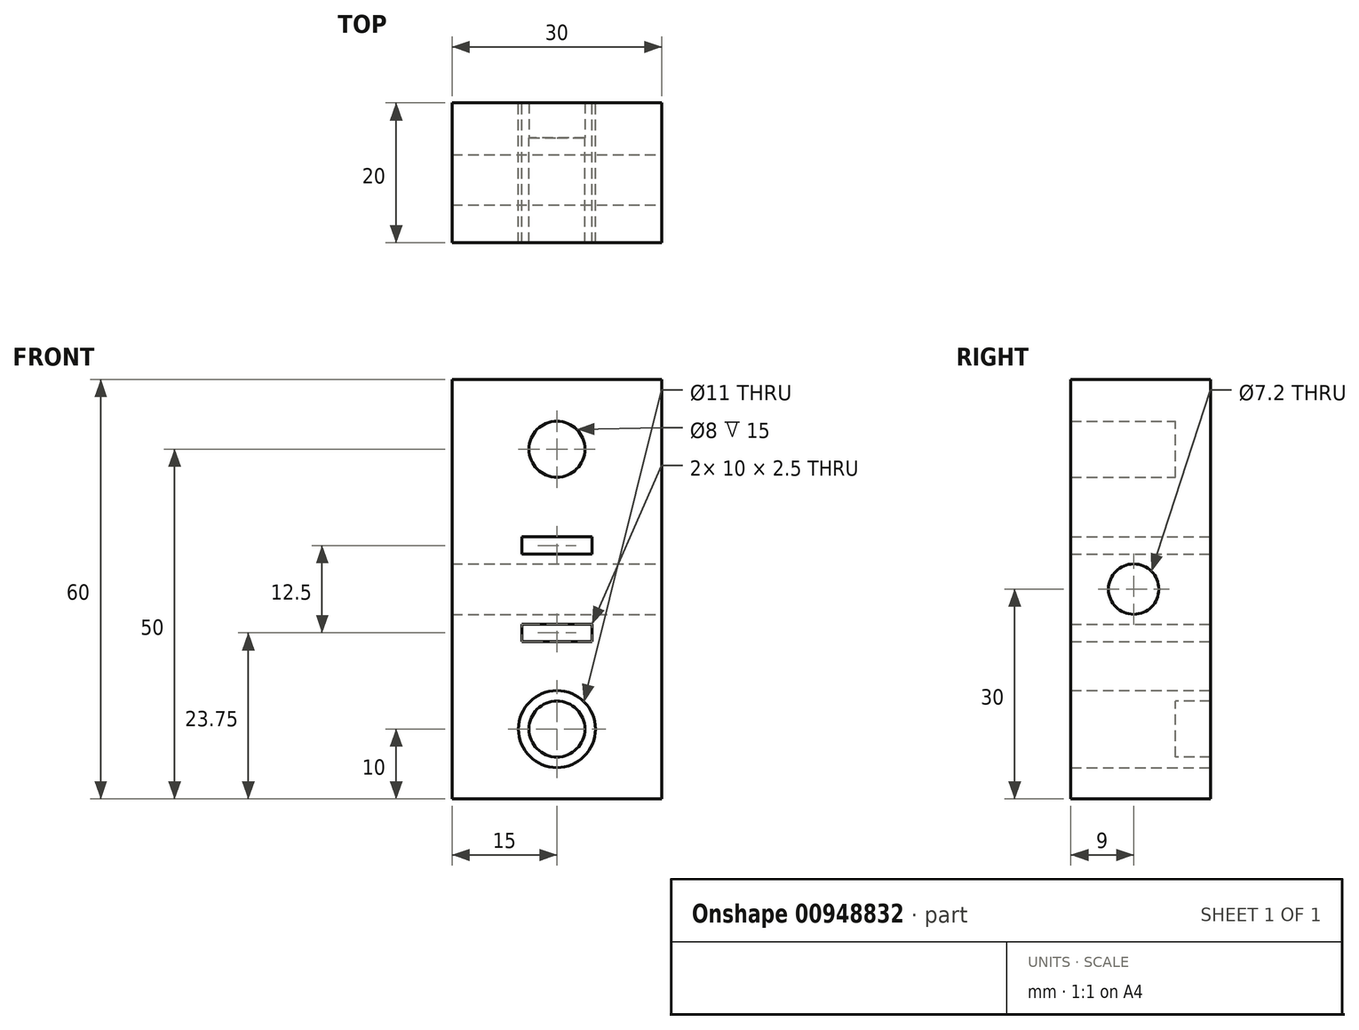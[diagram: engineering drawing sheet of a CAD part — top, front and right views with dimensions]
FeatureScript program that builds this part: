
annotation { "Feature Type Name" : "Feature", "Feature Type Description" : "" }
export const myFeature = defineFeature(function(context is Context, id is Id, definition is map)
    precondition{}
    {
        {
            var Q0;
            Q0=qCreatedBy(makeId("Front.planeOp"),FACE);
            var sketch = newSketch(context, id + "F0", { "sketchPlane" : qUnion([Q0])});
            skLineSegment(sketch, "E0.bottom", {"start": v(15, -30) * mm, "end": v(-15, -30) * mm});
            skLineSegment(sketch, "E0.top", {"start": v(15, 30) * mm, "end": v(-15, 30) * mm});
            skLineSegment(sketch, "E0.left", {"start": v(15, -30) * mm, "end": v(15, 30) * mm});
            skLineSegment(sketch, "E0.right", {"start": v(-15, -30) * mm, "end": v(-15, 30) * mm});
            skPoint(sketch, "E0.middle", {"position": v(0, 0) * mm});
            skCircle(sketch, "E1", {"center": v(0, 20) * mm, "radius": 5.5 * mm});
            skLineSegment(sketch, "E2.bottom", {"start": v(5, 5) * mm, "end": v(-5, 5) * mm});
            skLineSegment(sketch, "E2.top", {"start": v(5, 7.5) * mm, "end": v(-5, 7.5) * mm});
            skLineSegment(sketch, "E2.left", {"start": v(5, 5) * mm, "end": v(5, 7.5) * mm});
            skLineSegment(sketch, "E2.right", {"start": v(-5, 5) * mm, "end": v(-5, 7.5) * mm});
            skPoint(sketch, "E2.middle", {"position": v(0, 6.25) * mm});
            skLineSegment(sketch, "E3.MirrorCS", {"start": v(-5, -5) * mm, "end": v(-5, -7.5) * mm});
            skLineSegment(sketch, "E4.MirrorCS", {"start": v(5, -5) * mm, "end": v(5, -7.5) * mm});
            skLineSegment(sketch, "E5.MirrorCS", {"start": v(5, -7.5) * mm, "end": v(-5, -7.5) * mm});
            skLineSegment(sketch, "E6.MirrorCS", {"start": v(5, -5) * mm, "end": v(-5, -5) * mm});
            skCircle(sketch, "E7.MirrorC", {"center": v(0, -20) * mm, "radius": 5.5 * mm});
            skPoint(sketch, "E8.MirrorP", {"position": v(0, -6.25) * mm});
            skCircle(sketch, "E9", {"center": v(0, 20) * mm, "radius": 4 * mm});
            skCircle(sketch, "E10", {"center": v(0, -20) * mm, "radius": 4 * mm});
            skSolve(sketch);
        }
        {
            var Q0;
            Q0=makeQuery(id+"F0.imprint","IMPRINT",FACE,{"disambiguationData":[TD([[makeQuery(id+"F0.imprint","IMPRINT",EDGE,{"derivedFrom":sQuery(id+"F0.wireOp",EDGE,"E0.bottom")}),-1.0]])]});
            var Q1;
            Q1=makeQuery(id+"F0.imprint","IMPRINT",FACE,{"disambiguationData":[TD([[makeQuery(id+"F0.imprint","IMPRINT",EDGE,{"derivedFrom":sQuery(id+"F0.wireOp",EDGE,"E1")}),1.0]])]});
            var Q2;
            Q2=makeQuery(id+"F0.imprint","IMPRINT",FACE,{"disambiguationData":[TD([[makeQuery(id+"F0.imprint","IMPRINT",EDGE,{"derivedFrom":sQuery(id+"F0.wireOp",EDGE,"E7.MirrorC")}),-1.0]])]});
            extrude(context, id + "F1", {"entities" : qUnion([Q0, Q1, Q2]), "depth" : 5 * mm, "offsetDistance" : 25 * mm});
        }
        {
            var Q0;
            Q0=makeQuery(id+"F0.imprint","IMPRINT",FACE,{"disambiguationData":[TD([[makeQuery(id+"F0.imprint","IMPRINT",EDGE,{"derivedFrom":sQuery(id+"F0.wireOp",EDGE,"E1")}),1.0]])]});
            var Q1;
            Q1=makeQuery(id+"F0.imprint","IMPRINT",FACE,{"disambiguationData":[TD([[makeQuery(id+"F0.imprint","IMPRINT",EDGE,{"derivedFrom":sQuery(id+"F0.wireOp",EDGE,"E7.MirrorC")}),-1.0]])]});
            var Q2;
            Q2=makeQuery(id+"F0.imprint","IMPRINT",FACE,{"disambiguationData":[TD([[makeQuery(id+"F0.imprint","IMPRINT",EDGE,{"derivedFrom":sQuery(id+"F0.wireOp",EDGE,"E9")}),1.0]])]});
            var Q3;
            Q3=makeQuery(id+"F0.imprint","IMPRINT",FACE,{"disambiguationData":[TD([[makeQuery(id+"F0.imprint","IMPRINT",EDGE,{"derivedFrom":sQuery(id+"F0.wireOp",EDGE,"E10")}),1.0]])]});
            var Q4;
            Q4=sQuery(id+"F0.wireOp",EDGE,"E1");
            var Q5;
            Q5=sQuery(id+"F0.wireOp",EDGE,"E7.MirrorC");
            extrude(context, id + "F2", {"entities" : qUnion([Q0, Q1, Q2, Q3]), "operationType" : NewBodyOperationType.ADD, "surfaceEntities" : qUnion([Q4, Q5]), "oppositeDirection" : true, "depth" : 15 * mm, "offsetDistance" : 25 * mm});
        }
        {
            var Q0;
            Q0=qCreatedBy(makeId("Right.planeOp"),FACE);
            var sketch = newSketch(context, id + "F3", { "sketchPlane" : qUnion([Q0])});
            skCircle(sketch, "E11", {"center": v(4, 0) * mm, "radius": 3.6 * mm});
            skLineSegment(sketch, "E12.bottom", {"start": v(0, 5) * mm, "end": v(10, 5) * mm});
            skLineSegment(sketch, "E12.top", {"start": v(0, -5) * mm, "end": v(10, -5) * mm});
            skLineSegment(sketch, "E12.left", {"start": v(0, 5) * mm, "end": v(0, -5) * mm});
            skLineSegment(sketch, "E12.right", {"start": v(10, 5) * mm, "end": v(10, -5) * mm});
            skSolve(sketch);
        }
        {
            var Q0;
            Q0=qSketchRegion(id+"F3",true);
            var Q1;
            Q1=makeQuery(id+"F3.imprint","IMPRINT",FACE,{"disambiguationData":[TD([[makeQuery(id+"F3.imprint","IMPRINT",EDGE,{"derivedFrom":sQuery(id+"F3.wireOp",EDGE,"E11")}),1.0]])]});
            extrude(context, id + "F4", {"entities" : qUnion([Q0, Q1]), "operationType" : NewBodyOperationType.ADD, "endBound" : BoundingType.SYMMETRIC, "depth" : 30 * mm, "offsetDistance" : 25 * mm});
        }
        {
            var Q0;
            Q0=makeQuery(id+"F3.imprint","IMPRINT",FACE,{"disambiguationData":[TD([[makeQuery(id+"F3.imprint","IMPRINT",EDGE,{"derivedFrom":sQuery(id+"F3.wireOp",EDGE,"E11")}),1.0]])]});
            extrude(context, id + "F5", {"entities" : qUnion([Q0]), "operationType" : NewBodyOperationType.REMOVE, "endBound" : BoundingType.SYMMETRIC, "oppositeDirection" : true, "depth" : 50 * mm, "offsetDistance" : 25 * mm});
        }
        {
            var Q0;
            Q0=makeQuery(id+"F0.imprint","IMPRINT",FACE,{"disambiguationData":[TD([[makeQuery(id+"F0.imprint","IMPRINT",EDGE,{"derivedFrom":sQuery(id+"F0.wireOp",EDGE,"E9")}),1.0]])]});
            var Q1;
            Q1=makeQuery(id+"F0.imprint","IMPRINT",FACE,{"disambiguationData":[TD([[makeQuery(id+"F0.imprint","IMPRINT",EDGE,{"derivedFrom":sQuery(id+"F0.wireOp",EDGE,"E10")}),1.0]])]});
            extrude(context, id + "F6", {"entities" : qUnion([Q0, Q1]), "operationType" : NewBodyOperationType.REMOVE, "endBound" : BoundingType.SYMMETRIC, "oppositeDirection" : true, "depth" : 20 * mm, "offsetDistance" : 25 * mm});
        }
    });
